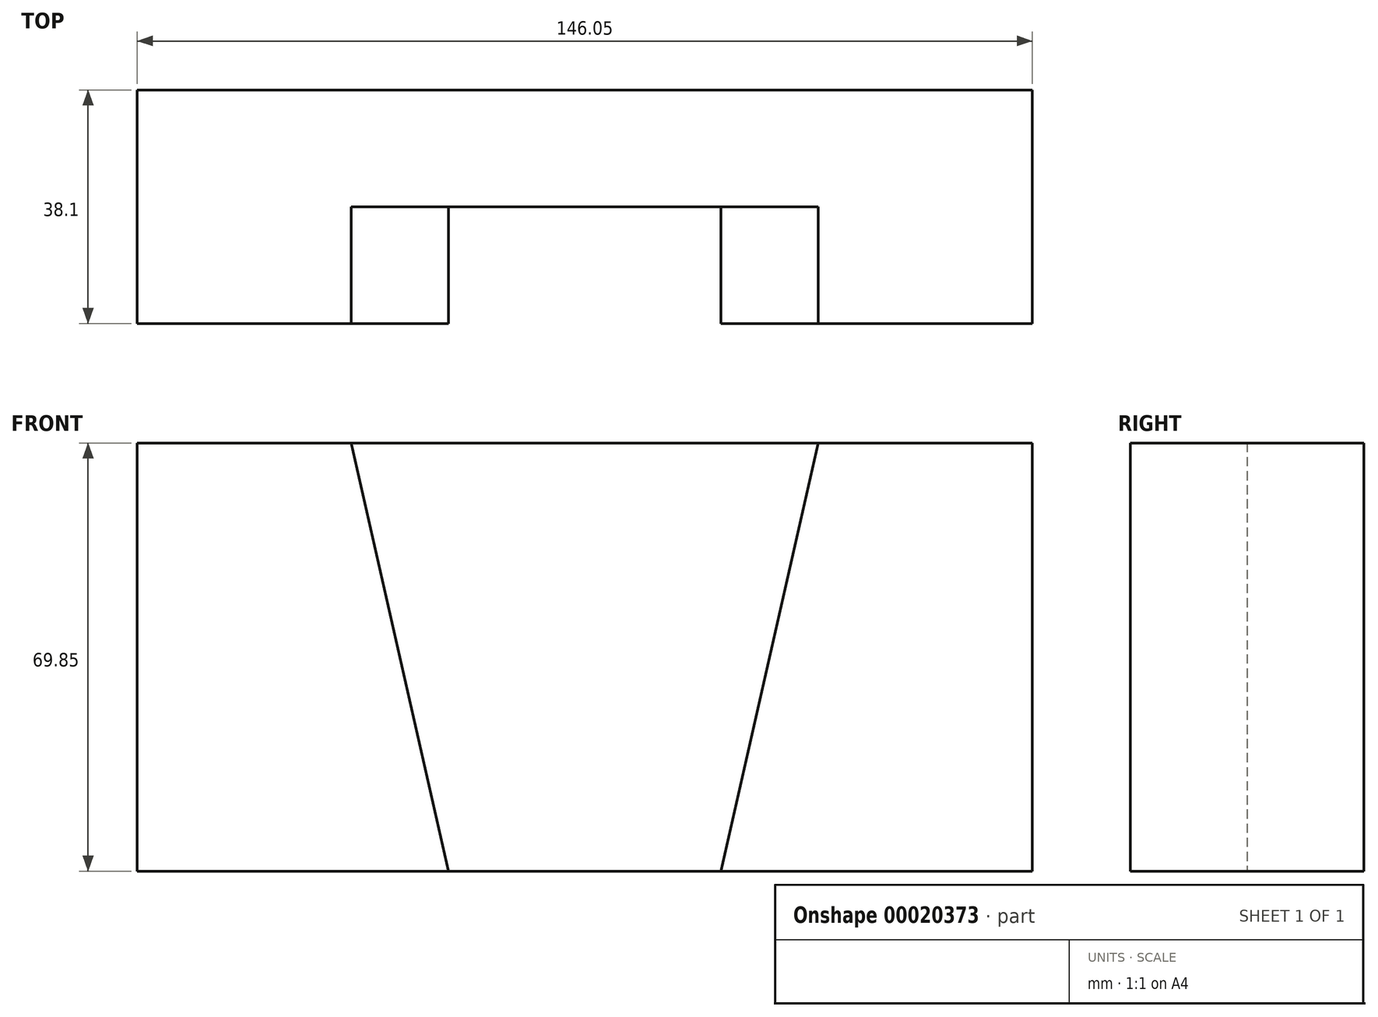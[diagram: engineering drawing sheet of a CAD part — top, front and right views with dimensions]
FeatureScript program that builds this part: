
annotation { "Feature Type Name" : "Feature", "Feature Type Description" : "" }
export const myFeature = defineFeature(function(context is Context, id is Id, definition is map)
    precondition{}
    {
        {
            var Q0;
            Q0=qCreatedBy(makeId("Front.planeOp"),FACE);
            var sketch = newSketch(context, id + "F0", { "sketchPlane" : qUnion([Q0])});
            skLineSegment(sketch, "E0.bottom", {"start": v(-80.77, 29.6) * mm, "end": v(65.28, 29.6) * mm});
            skLineSegment(sketch, "E0.top", {"start": v(-80.77, -40.25) * mm, "end": v(65.28, -40.25) * mm});
            skLineSegment(sketch, "E0.left", {"start": v(-80.77, 29.6) * mm, "end": v(-80.77, -40.25) * mm});
            skLineSegment(sketch, "E0.right", {"start": v(65.28, 29.6) * mm, "end": v(65.28, -40.25) * mm});
            skSolve(sketch);
        }
        {
            var Q0;
            Q0=makeQuery(id+"F0.imprint","IMPRINT",FACE,{"disambiguationData":[TD([[makeQuery(id+"F0.imprint","IMPRINT",EDGE,{"derivedFrom":sQuery(id+"F0.wireOp",EDGE,"E0.bottom")}),-1.0]])]});
            extrude(context, id + "F1", {"entities" : qUnion([Q0]), "depth" : 38.1 * mm});
        }
        {
            var Q0;
            Q0=makeQuery(id+"F1.opExtrude","CAP_FACE",FACE,{"disambiguationData":[OSD([sQuery(id+"F0.wireOp",EDGE,"E0.bottom"),sQuery(id+"F0.wireOp",EDGE,"E0.top"),sQuery(id+"F0.wireOp",EDGE,"E0.left"),sQuery(id+"F0.wireOp",EDGE,"E0.right")])],"isStart":false});
            var sketch = newSketch(context, id + "F2", { "sketchPlane" : qUnion([Q0])});
            skLineSegment(sketch, "E1", {"start": v(-45.85, 29.6) * mm, "end": v(30.35, 29.6) * mm});
            skLineSegment(sketch, "E2", {"start": v(30.35, 29.6) * mm, "end": v(14.48, -40.25) * mm});
            skLineSegment(sketch, "E3", {"start": v(14.48, -40.25) * mm, "end": v(-29.97, -40.25) * mm});
            skLineSegment(sketch, "E4", {"start": v(-29.97, -40.25) * mm, "end": v(-45.85, 29.6) * mm});
            skLineSegment(sketch, "E5", {"start": v(-45.85, 29.6) * mm, "end": v(-80.77, 29.6) * mm});
            skLineSegment(sketch, "E6", {"start": v(14.48, -40.25) * mm, "end": v(65.28, -40.25) * mm});
            skSolve(sketch);
        }
        {
            var Q0;
            Q0=makeQuery(id+"F2.imprint","IMPRINT",FACE,{"disambiguationData":[TD([[makeQuery(id+"F2.imprint","IMPRINT",EDGE,{"derivedFrom":sQuery(id+"F2.wireOp",EDGE,"E1")}),-1.0]])]});
            extrude(context, id + "F3", {"entities" : qUnion([Q0]), "operationType" : NewBodyOperationType.REMOVE, "oppositeDirection" : true, "depth" : 19.05 * mm});
        }
    });
